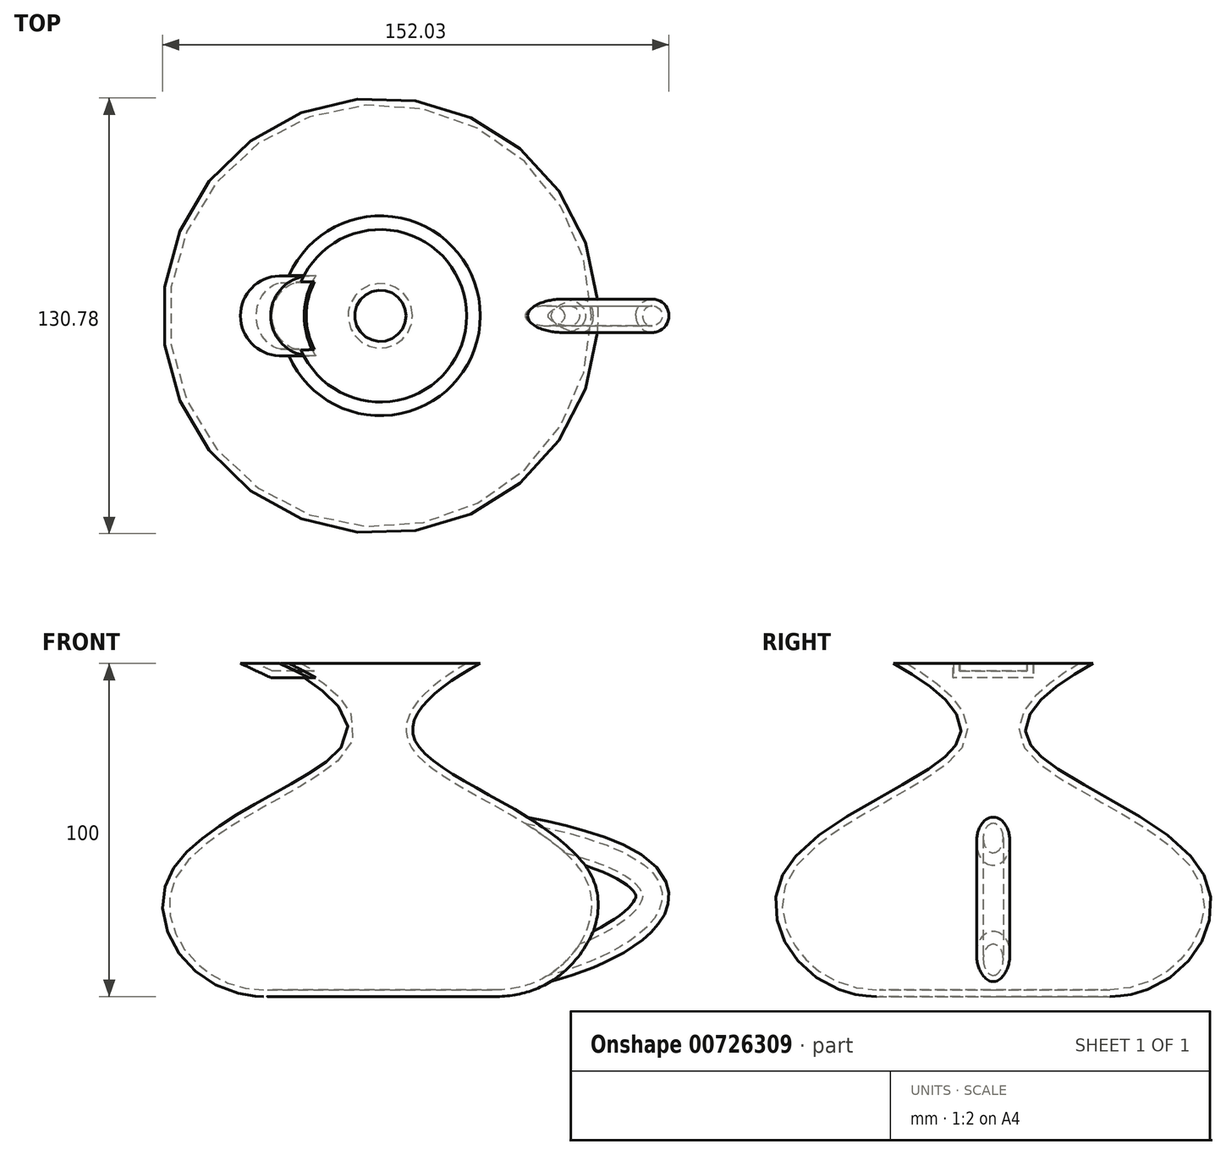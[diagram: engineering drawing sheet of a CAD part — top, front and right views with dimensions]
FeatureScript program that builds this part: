
annotation { "Feature Type Name" : "Feature", "Feature Type Description" : "" }
export const myFeature = defineFeature(function(context is Context, id is Id, definition is map)
    precondition{}
    {
        {
            var Q0;
            Q0=qCreatedBy(makeId("Front.planeOp"),FACE);
            var sketch = newSketch(context, id + "F0", { "sketchPlane" : qUnion([Q0])});
            skLineSegment(sketch, "E0", {"start": v(0, 49.55) * mm, "end": v(30, 49.55) * mm});
            skLineSegment(sketch, "E1", {"start": v(0, -50.45) * mm, "end": v(35, -50.45) * mm});
            skFitSpline(sketch, "E2", {"points": [v(30, 49.55) * mm, v(10.42, 26.44) * mm, v(63.76, -15) * mm, v(35, -50.45) * mm], "startDerivative": vector(-132.49, -71.8) * mm, "endDerivative": vector(-189.58, 0) * mm});
            skLineSegment(sketch, "E3", {"start": v(0, 49.55) * mm, "end": v(0, -50.45) * mm});
            skSolve(sketch);
        }
        {
            var Q0;
            Q0 = qSketchRegion(id + "F0", true);
            var Q1;
            Q1=sQuery(id+"F0.wireOp",EDGE,"E3");
            revolve(context, id + "F1", {"surfaceOperationType" : NewSurfaceOperationType.NEW, "entities" : qUnion([Q0]), "axis" : qUnion([Q1]), "revolveType" : RevolveType.FULL});
        }
        {
            var Q0;
            Q0=qCreatedBy(makeId("Front.planeOp"),FACE);
            var sketch = newSketch(context, id + "F2", { "sketchPlane" : qUnion([Q0])});
            skFitSpline(sketch, "E4", {"points": [v(0, 4) * mm, v(81.44, -21.98) * mm, v(0, -44) * mm], "startDerivative": vector(304.72, -23.92) * mm, "endDerivative": vector(-233.24, 36.54) * mm});
            skSolve(sketch);
        }
        {
            var Q0;
            Q0=qCreatedBy(makeId("Right.planeOp"),FACE);
            var sketch = newSketch(context, id + "F3", { "sketchPlane" : qUnion([Q0])});
            skCircle(sketch, "E5", {"center": v(0, 4) * mm, "radius": 5 * mm});
            skSolve(sketch);
        }
        {
            var Q0;
            Q0 = qSketchRegion(id + "F3", true);
            var Q1;
            Q1 = qConstructionFilter(qBodyType(qCreatedBy(id + "F2" ,EDGE), BodyType.WIRE), ConstructionObject.NO);
            sweep(context, id + "F4", {"operationType" : NewBodyOperationType.ADD, "profiles" : qUnion([Q0]), "path" : qUnion([Q1])});
        }
        {
            var Q0;
            Q0=makeQuery(id+"F1.opRevolve","SWEPT_FACE",FACE,{"disambiguationData":[OSD([sQuery(id+"F0.wireOp",EDGE,"E0")])]});
            var sketch = newSketch(context, id + "F5", { "sketchPlane" : qUnion([Q0])});
            skArc(sketch, "E6", {"start": v(-42, 0) * mm, "mid": v(-38.62, -8.34) * mm, "end": v(-30.4, -12) * mm});
            skLineSegment(sketch, "E7", {"start": v(0, 0) * mm, "end": v(0, -13) * mm});
            skLineSegment(sketch, "E8", {"start": v(0, -13) * mm, "end": v(-30.4, -12) * mm});
            skArc(sketch, "E9.MirrorCS", {"start": v(-42, 0) * mm, "mid": v(-38.62, 8.34) * mm, "end": v(-30.4, 12) * mm});
            skLineSegment(sketch, "E10.MirrorCS", {"start": v(0, 13) * mm, "end": v(-30.4, 12) * mm});
            skLineSegment(sketch, "E11.MirrorCS", {"start": v(0, 0) * mm, "end": v(0, 13) * mm});
            skSolve(sketch);
        }
        {
            var Q0;
            Q0=qCreatedBy(makeId("Front.planeOp"),FACE);
            var sketch = newSketch(context, id + "F6", { "sketchPlane" : qUnion([Q0])});
            skLineSegment(sketch, "E12", {"start": v(0, 49.55) * mm, "end": v(9.06, 45.32) * mm});
            skSolve(sketch);
        }
        {
            var Q0;
            Q0 = qSketchRegion(id + "F5", true);
            var Q1;
            Q1 = qConstructionFilter(qBodyType(qCreatedBy(id + "F6" ,EDGE), BodyType.WIRE), ConstructionObject.NO);
            sweep(context, id + "F7", {"operationType" : NewBodyOperationType.ADD, "profiles" : qUnion([Q0]), "path" : qUnion([Q1])});
        }
        {
            var Q0;
            Q0=makeQuery(id+"F7.boolean.opBoolean","MERGE",FACE,{"derivedFrom":[makeQuery(id+"F1.opRevolve","SWEPT_FACE",FACE,{"disambiguationData":[OSD([sQuery(id+"F0.wireOp",EDGE,"E0")])]}),makeQuery(id+"F7.opSweep","CAP_FACE",FACE,{"disambiguationData":[OSD([sQuery(id+"F5.wireOp",EDGE,"E6"),sQuery(id+"F5.wireOp",EDGE,"E7"),sQuery(id+"F5.wireOp",EDGE,"E8"),sQuery(id+"F5.wireOp",EDGE,"E9.MirrorCS"),sQuery(id+"F5.wireOp",EDGE,"E10.MirrorCS"),sQuery(id+"F5.wireOp",EDGE,"E11.MirrorCS"),sQuery(id+"F6.wireOp",VERTEX,"E12.start")])],"isStart":true})]});
            shell(context, id + "F8", {"entities" : qUnion([Q0]), "thickness" : 2 * mm});
        }
    });
